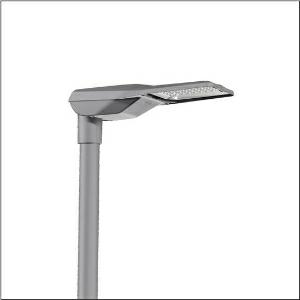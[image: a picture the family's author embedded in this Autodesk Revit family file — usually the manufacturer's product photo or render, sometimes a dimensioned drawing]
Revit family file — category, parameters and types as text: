
# Revit family: streetlight_sl_21_iq_mini___st1_0ab_5xe2m31g08hb_98c3
name_source: partatom
category: Lighting Fixtures
units: mm (PartAtom-declared; Revit-internal decimal feet)

## family parameters
Cut with Voids When Loaded = No
Host = Face
Light Source = No
Part Type = Normal
Room Calculation Point = No
Round Connector Dimension = Use Diameter
Shared = No

## types (1)
- --- (1 x LED, 8320 lm, 70.9 W, 3000K)
    Apparent Load = 71 VA
    CIE Flux Codes = 38 73 97 100 100
    Color Rendering = 70
    Color Temperature = 3000K
    Default Elevation = 1800 mm
    Description = Streetlight SL 21 iQ mini, mast luminaire, primary light control with lens, of PMMA, primary optical cover: cover, of toughened safety glass, transparent, light distribution: ST1.0aB, light emission: direct distribution, primary light characteristic: asymmetric, installation type: post-top, side-entry, LED, High Power LED, rated luminous flux: 8.320lm, luminous efficacy: 117lm/W, light colour: 730, colour temperature: 3000K, control gear: iQ Street-Remote, control: Street-Remote, Auto-Match, Temp-Guard, Lumen-Switch, Night-Set, Smart-Wire, Light-Fading, Desk-Remote (wireless, voltage-free reading and setting of iQ features in the workshop via application-optimized NFC function/RFID function), optimised constant luminous flux control (CLO 2.0), pre-setting: linear dimming characteristic, mains connection: 220..240V, AC, 50/60Hz, start of lifetime: 71W, end of service life: 75W, reduction: 31W, luminaire housing, of diecast aluminium, powder-coated, SITECO metallic grey (DB 702S), corrosivity category C5 high according to DIN EN ISO 12944, please order mast flange separately, inclination adjustable: 0°, 5°, 10°, 15°, sealing non-destructively replaceable, multi-level sealing system, length: 628mm, width: 235mm, height: 110mm, mast flange for spigot size: 42mm (side-entry): 5XC10008XM4, 60/48mm (side-entry/post-top): 5XC10108XM2, 76/60mm (side-entry/post-top): 5XC10108XM1, mounting height: 4..8m, protection rating (complete): IP66, insulation class (complete): insulation class II (safety insulation), certification: CE, ENEC, ENEC+, VDE, impact resistance: IK10, permissible operating ambient temperature for outdoor applications: -40..+50°C, standard-compliant lighting for roads and squares, packaging unit: 1 piece

Light Distribution: ST1.0aB
    Height = 110 mm
    Lamp = 1 x LED
    Lamp Light Flux = 8320 lm
    Lamp Power = 70.9 W
    Lamp count = 1
    Length = 625 mm
    Luminous efficacy = 117 lm/W
    Manufacturer = Siteco
    ModVariant = No
    Model = 5XE2M31G08HB
    Number of Poles = 1
    OnlyDefault = Yes
    Power Factor = 1
    Product Name = Streetlight SL 21 iQ mini | ST1.0aB
    Product group = mast luminaire | pylon top
    ProductGroupID = 6100
    Protection Class = Protection class II
    Protection Degree = IP 66
    RLX_Detail_Level = 1
    RLX_Emergency_Light_Flux = 0 lm
    RLX_Emergency_Type = 0
    RLX_Emergency_Type_DB = No
    RlxData = <blob elided: 26281 chars, md5=1bbc29d3>
    Socket = socket
    Standby Power = 0 W
    System Light Flux = 8320 lm
    System Power = 71 W
    Type Comments = factory setting: luminous flux: 100 % | dim-lin: 254 | 711 mA
    Type Image = l_1003519.jpg
    URL = http://relux.com
    VarID = @adj_156615
    Voltage = 0 V
    Weight = 0.00 kg
    Width = 234 mm

## geometry (parser evidence)
native form markers: Blend x4, Sweep x11
no freeform markers — native parametric forms only
